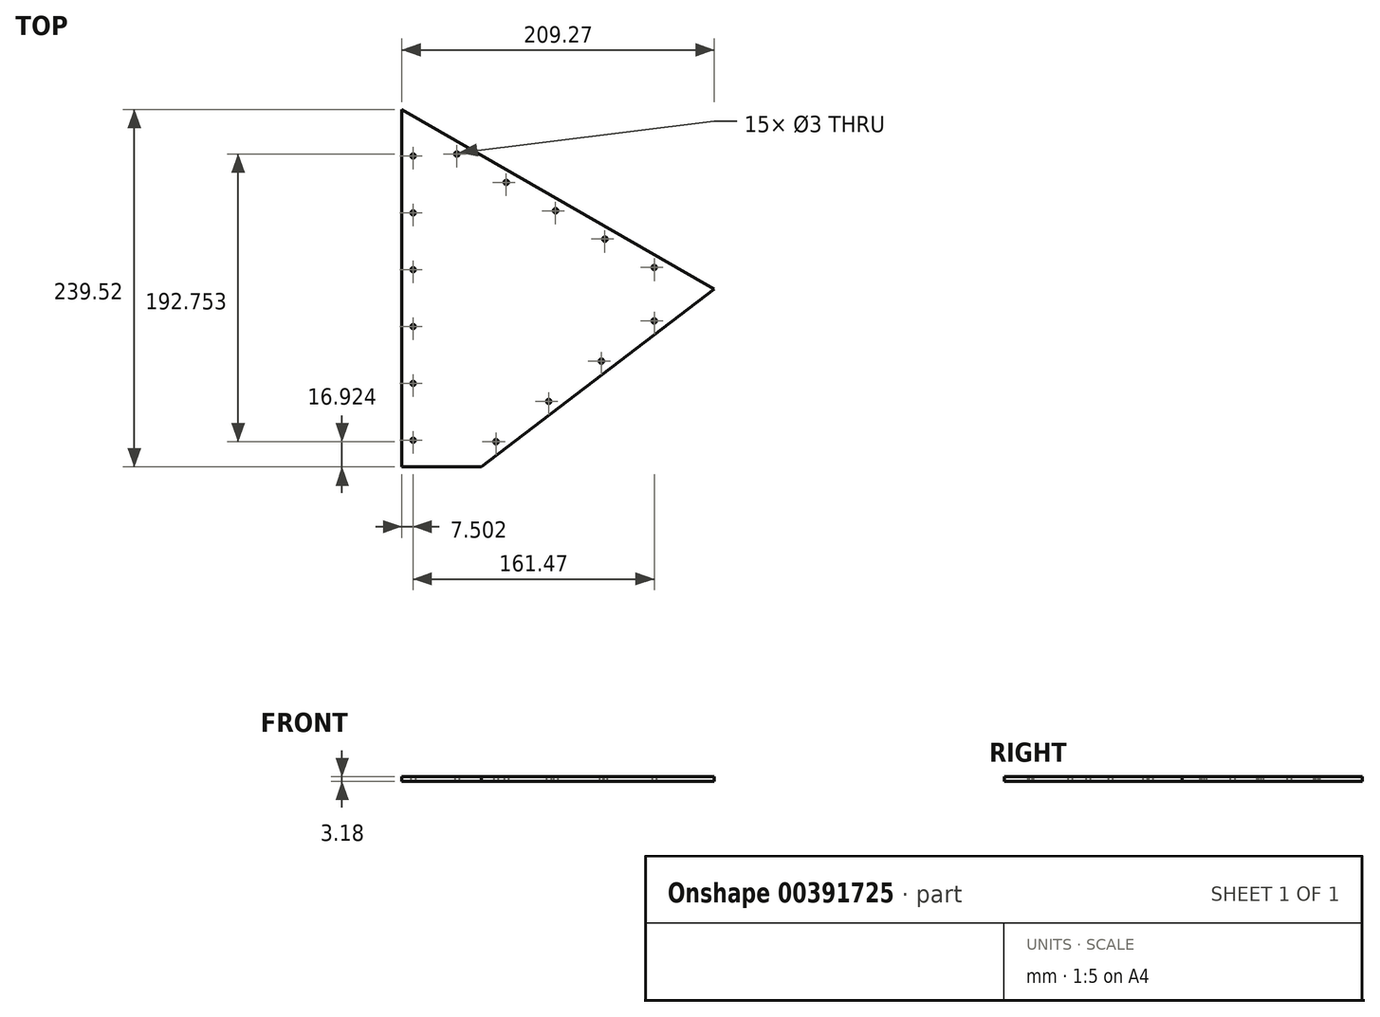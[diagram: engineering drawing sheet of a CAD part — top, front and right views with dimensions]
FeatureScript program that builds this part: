
annotation { "Feature Type Name" : "Feature", "Feature Type Description" : "" }
export const myFeature = defineFeature(function(context is Context, id is Id, definition is map)
    precondition{}
    {
        {
            var Q0;
            Q0=qCreatedBy(makeId("Top.planeOp"),FACE);
            var sketch = newSketch(context, id + "F0", { "sketchPlane" : qUnion([Q0])});
            skLineSegment(sketch, "E0", {"start": v(-223.28, 109.14) * mm, "end": v(256.18, 164.08) * mm});
            skLineSegment(sketch, "E1", {"start": v(-223.28, 109.14) * mm, "end": v(-223.28, -202.01) * mm});
            skLineSegment(sketch, "E2", {"start": v(-223.28, -202.01) * mm, "end": v(256.18, 164.08) * mm});
            skLineSegment(sketch, "E3", {"start": v(-223.28, -202.01) * mm, "end": v(-223.28, 81.44) * mm, "construction": true});
            skSolve(sketch);
        }
        {
            var Q0;
            Q0=qCreatedBy(makeId("Top.planeOp"),FACE);
            var sketch = newSketch(context, id + "F1", { "sketchPlane" : qUnion([Q0])});
            skPoint(sketch, "E4.visualSharp", {"position": v(-223.28, -202.01) * mm});
            skCircle(sketch, "E5", {"center": v(-198.42, -128.65) * mm, "radius": 8 * mm});
            skLineSegment(sketch, "E6.0", {"start": v(-170.1, -161.41) * mm, "end": v(-14.01, -42.23) * mm});
            skLineSegment(sketch, "E7", {"start": v(-170.1, -161.41) * mm, "end": v(-223.28, -161.41) * mm});
            skLineSegment(sketch, "E8", {"start": v(-223.28, -161.41) * mm, "end": v(-223.28, 78.11) * mm});
            skLineSegment(sketch, "E9", {"start": v(-223.28, 78.11) * mm, "end": v(-14.01, -42.23) * mm});
            skPoint(sketch, "E10.orphan", {"position": v(256.18, 164.08) * mm});
            skLineSegment(sketch, "E11.0", {"start": v(-175.18, -146.41) * mm, "end": v(-41.04, -44) * mm});
            skLineSegment(sketch, "E11.1", {"start": v(-175.18, -146.41) * mm, "end": v(-208.28, -146.41) * mm});
            skLineSegment(sketch, "E11.2", {"start": v(-208.28, -146.41) * mm, "end": v(-208.28, 52.18) * mm});
            skLineSegment(sketch, "E11.3", {"start": v(-208.28, 52.18) * mm, "end": v(-41.04, -44) * mm});
            skCircle(sketch, "E12.1.0.0", {"center": v(-182.83, -119.65) * mm, "radius": 8 * mm});
            skCircle(sketch, "E12.2.0.0", {"center": v(-167.24, -110.65) * mm, "radius": 8 * mm});
            skCircle(sketch, "E12.3.0.0", {"center": v(-151.65, -101.65) * mm, "radius": 8 * mm});
            skCircle(sketch, "E12.4.0.0", {"center": v(-136.06, -92.65) * mm, "radius": 8 * mm});
            skCircle(sketch, "E12.5.0.0", {"center": v(-120.47, -83.65) * mm, "radius": 8 * mm});
            skCircle(sketch, "E12.6.0.0", {"center": v(-104.89, -74.65) * mm, "radius": 8 * mm});
            skCircle(sketch, "E12.7.0.0", {"center": v(-89.3, -65.65) * mm, "radius": 8 * mm});
            skLineSegment(sketch, "E12.direction1", {"start": v(-198.42, -128.65) * mm, "end": v(-182.83, -119.65) * mm, "construction": true});
            skCircle(sketch, "E13.1.0.0", {"center": v(-198.42, -110.65) * mm, "radius": 8 * mm});
            skCircle(sketch, "E13.2.0.0", {"center": v(-182.83, -101.65) * mm, "radius": 8 * mm});
            skCircle(sketch, "E13.3.0.0", {"center": v(-167.24, -92.65) * mm, "radius": 8 * mm});
            skCircle(sketch, "E13.4.0.0", {"center": v(-151.65, -83.65) * mm, "radius": 8 * mm});
            skCircle(sketch, "E13.5.0.0", {"center": v(-136.06, -74.65) * mm, "radius": 8 * mm});
            skCircle(sketch, "E13.6.0.0", {"center": v(-120.47, -65.65) * mm, "radius": 8 * mm});
            skCircle(sketch, "E13.7.0.0", {"center": v(-104.89, -56.65) * mm, "radius": 8 * mm});
            skCircle(sketch, "E14.1.0.0", {"center": v(-198.42, -92.65) * mm, "radius": 8 * mm});
            skCircle(sketch, "E14.2.0.0", {"center": v(-182.83, -83.65) * mm, "radius": 8 * mm});
            skCircle(sketch, "E14.3.0.0", {"center": v(-167.24, -74.65) * mm, "radius": 8 * mm});
            skCircle(sketch, "E14.4.0.0", {"center": v(-151.65, -65.65) * mm, "radius": 8 * mm});
            skCircle(sketch, "E14.5.0.0", {"center": v(-136.06, -56.65) * mm, "radius": 8 * mm});
            skCircle(sketch, "E14.6.0.0", {"center": v(-120.47, -47.65) * mm, "radius": 8 * mm});
            skCircle(sketch, "E15", {"center": v(-198.42, -74.65) * mm, "radius": 8 * mm});
            skCircle(sketch, "E16.1.0.0", {"center": v(-182.83, -65.65) * mm, "radius": 8 * mm});
            skCircle(sketch, "E16.2.0.0", {"center": v(-167.24, -56.65) * mm, "radius": 8 * mm});
            skCircle(sketch, "E16.3.0.0", {"center": v(-151.65, -47.65) * mm, "radius": 8 * mm});
            skCircle(sketch, "E16.4.0.0", {"center": v(-136.06, -38.65) * mm, "radius": 8 * mm});
            skCircle(sketch, "E16.5.0.0", {"center": v(-120.47, -29.65) * mm, "radius": 8 * mm});
            skCircle(sketch, "E17", {"center": v(-198.42, -56.65) * mm, "radius": 8 * mm});
            skCircle(sketch, "E18.1.0.0", {"center": v(-182.83, -47.65) * mm, "radius": 8 * mm});
            skCircle(sketch, "E18.2.0.0", {"center": v(-167.24, -38.65) * mm, "radius": 8 * mm});
            skCircle(sketch, "E18.3.0.0", {"center": v(-151.65, -29.65) * mm, "radius": 8 * mm});
            skCircle(sketch, "E18.4.0.0", {"center": v(-136.06, -20.65) * mm, "radius": 8 * mm});
            skCircle(sketch, "E19", {"center": v(-198.42, -38.65) * mm, "radius": 8 * mm});
            skCircle(sketch, "E20.1.0.0", {"center": v(-182.83, -29.65) * mm, "radius": 8 * mm});
            skCircle(sketch, "E20.2.0.0", {"center": v(-167.24, -20.65) * mm, "radius": 8 * mm});
            skCircle(sketch, "E20.3.0.0", {"center": v(-151.65, -11.65) * mm, "radius": 8 * mm});
            skCircle(sketch, "E21", {"center": v(-198.42, -20.65) * mm, "radius": 8 * mm});
            skCircle(sketch, "E22.1.0.0", {"center": v(-182.83, -11.65) * mm, "radius": 8 * mm});
            skCircle(sketch, "E22.2.0.0", {"center": v(-167.24, -2.65) * mm, "radius": 8 * mm});
            skCircle(sketch, "E22.3.0.0", {"center": v(-151.65, 6.35) * mm, "radius": 8 * mm});
            skLineSegment(sketch, "E23", {"start": v(-198.42, -128.65) * mm, "end": v(-198.42, -110.65) * mm});
            skLineSegment(sketch, "E24", {"start": v(-198.42, -92.65) * mm, "end": v(-198.42, -110.65) * mm});
            skLineSegment(sketch, "E25", {"start": v(-198.42, -92.65) * mm, "end": v(-198.42, -74.65) * mm});
            skLineSegment(sketch, "E26", {"start": v(-198.42, -56.65) * mm, "end": v(-198.42, -38.65) * mm});
            skLineSegment(sketch, "E27", {"start": v(-198.42, -20.65) * mm, "end": v(-182.83, -29.65) * mm});
            skLineSegment(sketch, "E28", {"start": v(-198.42, -38.65) * mm, "end": v(-198.42, -20.65) * mm});
            skLineSegment(sketch, "E29", {"start": v(-198.42, -56.65) * mm, "end": v(-198.42, -74.65) * mm});
            skLineSegment(sketch, "E30", {"start": v(-182.83, -119.65) * mm, "end": v(-182.83, -101.65) * mm});
            skLineSegment(sketch, "E31", {"start": v(-182.83, -83.65) * mm, "end": v(-182.83, -65.65) * mm});
            skLineSegment(sketch, "E32", {"start": v(-182.83, -47.65) * mm, "end": v(-182.83, -29.65) * mm});
            skLineSegment(sketch, "E33", {"start": v(-182.83, -11.65) * mm, "end": v(-182.83, -29.65) * mm});
            skLineSegment(sketch, "E34", {"start": v(-182.83, -11.65) * mm, "end": v(-167.24, -20.65) * mm});
            skLineSegment(sketch, "E35", {"start": v(-167.24, -38.65) * mm, "end": v(-167.24, -20.65) * mm});
            skLineSegment(sketch, "E36", {"start": v(-167.24, -38.65) * mm, "end": v(-167.24, -56.65) * mm});
            skLineSegment(sketch, "E37", {"start": v(-167.24, -56.65) * mm, "end": v(-167.24, -74.65) * mm});
            skLineSegment(sketch, "E38", {"start": v(-167.24, -74.65) * mm, "end": v(-167.24, -92.65) * mm});
            skLineSegment(sketch, "E39", {"start": v(-167.24, -92.65) * mm, "end": v(-167.24, -110.65) * mm});
            skLineSegment(sketch, "E40", {"start": v(-182.83, -101.65) * mm, "end": v(-182.83, -83.65) * mm});
            skLineSegment(sketch, "E41", {"start": v(-182.83, -65.65) * mm, "end": v(-182.83, -47.65) * mm});
            skLineSegment(sketch, "E42", {"start": v(-198.42, -110.65) * mm, "end": v(-182.83, -119.65) * mm});
            skLineSegment(sketch, "E43", {"start": v(-151.65, 6.35) * mm, "end": v(-151.65, -101.65) * mm});
            skLineSegment(sketch, "E44", {"start": v(-167.24, -2.65) * mm, "end": v(-120.47, -29.65) * mm});
            skLineSegment(sketch, "E45", {"start": v(-167.24, -2.65) * mm, "end": v(-167.24, -20.65) * mm});
            skLineSegment(sketch, "E46", {"start": v(-136.06, -20.65) * mm, "end": v(-136.06, -92.65) * mm});
            skLineSegment(sketch, "E47", {"start": v(-198.42, -110.65) * mm, "end": v(-104.89, -56.65) * mm});
            skLineSegment(sketch, "E48", {"start": v(-182.83, -11.65) * mm, "end": v(-89.3, -65.65) * mm});
            skLineSegment(sketch, "E49", {"start": v(-198.42, -92.65) * mm, "end": v(-120.47, -47.65) * mm});
            skLineSegment(sketch, "E50", {"start": v(-198.42, -74.65) * mm, "end": v(-120.47, -29.65) * mm});
            skLineSegment(sketch, "E51", {"start": v(-120.47, -29.65) * mm, "end": v(-120.47, -83.65) * mm});
            skLineSegment(sketch, "E52", {"start": v(-198.42, -56.65) * mm, "end": v(-136.06, -20.65) * mm});
            skLineSegment(sketch, "E53", {"start": v(-198.42, -128.65) * mm, "end": v(-89.3, -65.65) * mm});
            skLineSegment(sketch, "E54", {"start": v(-198.42, -38.65) * mm, "end": v(-151.65, -11.65) * mm});
            skLineSegment(sketch, "E55", {"start": v(-198.42, -20.65) * mm, "end": v(-151.65, 6.35) * mm});
            skCircle(sketch, "E56", {"center": v(-198.42, -2.65) * mm, "radius": 8 * mm});
            skCircle(sketch, "E57.1.0.0", {"center": v(-182.83, 6.35) * mm, "radius": 8 * mm});
            skCircle(sketch, "E57.2.0.0", {"center": v(-167.24, 15.35) * mm, "radius": 8 * mm});
            skCircle(sketch, "E58", {"center": v(-198.42, 15.35) * mm, "radius": 8 * mm});
            skCircle(sketch, "E59.1.0.0", {"center": v(-182.83, 24.35) * mm, "radius": 8 * mm});
            skCircle(sketch, "E59.3.0.0", {"center": v(-198.42, 33.35) * mm, "radius": 8 * mm});
            skLineSegment(sketch, "E60", {"start": v(-198.42, 33.35) * mm, "end": v(-198.42, -38.65) * mm});
            skLineSegment(sketch, "E61", {"start": v(-198.42, -2.65) * mm, "end": v(-182.83, -11.65) * mm});
            skLineSegment(sketch, "E62", {"start": v(-198.42, 15.35) * mm, "end": v(-167.24, -2.65) * mm});
            skLineSegment(sketch, "E63", {"start": v(-198.42, 33.35) * mm, "end": v(-151.65, 6.35) * mm});
            skLineSegment(sketch, "E64", {"start": v(-198.42, 15.35) * mm, "end": v(-182.83, 24.35) * mm});
            skCircle(sketch, "E65.5.0.0", {"center": v(-73.7, -56.65) * mm, "radius": 8 * mm});
            skCircle(sketch, "E66.4.0.0", {"center": v(-89.3, -47.65) * mm, "radius": 8 * mm});
            skCircle(sketch, "E67.3.0.0", {"center": v(-104.89, -38.65) * mm, "radius": 8 * mm});
            skLineSegment(sketch, "E68", {"start": v(-120.47, -29.65) * mm, "end": v(-73.7, -56.65) * mm});
            skLineSegment(sketch, "E69", {"start": v(-104.89, -38.65) * mm, "end": v(-120.47, -47.65) * mm});
            skLineSegment(sketch, "E70", {"start": v(-89.3, -47.65) * mm, "end": v(-104.89, -56.65) * mm});
            skLineSegment(sketch, "E71", {"start": v(-198.42, -2.65) * mm, "end": v(-167.24, 15.35) * mm});
            skLineSegment(sketch, "E72", {"start": v(-73.7, -56.65) * mm, "end": v(-89.3, -65.65) * mm});
            skCircle(sketch, "E73.3.0.0", {"center": v(-120.47, -11.65) * mm, "radius": 8 * mm});
            skCircle(sketch, "E74.2.0.0", {"center": v(-136.06, -2.65) * mm, "radius": 8 * mm});
            skLineSegment(sketch, "E75", {"start": v(-120.47, -11.65) * mm, "end": v(-151.65, 6.35) * mm});
            skLineSegment(sketch, "E76", {"start": v(-120.47, -11.65) * mm, "end": v(-120.47, -29.65) * mm});
            skLineSegment(sketch, "E77", {"start": v(-136.06, -2.65) * mm, "end": v(-136.06, -20.65) * mm});
            skSolve(sketch);
        }
        {
            var Q0;
            Q0=makeQuery(id+"F0.imprint","IMPRINT",FACE,{"disambiguationData":[TD([[makeQuery(id+"F0.imprint","IMPRINT",EDGE,{"derivedFrom":sQuery(id+"F0.wireOp",EDGE,"E0")}),-1.0]])]});
            var sketch = newSketch(context, id + "F2", { "sketchPlane" : qUnion([Q0])});
            skLineSegment(sketch, "E78.0", {"start": v(-223.28, 78.11) * mm, "end": v(-14.01, -42.23) * mm});
            skLineSegment(sketch, "E79.0", {"start": v(-223.28, -161.41) * mm, "end": v(-223.28, 78.11) * mm});
            skLineSegment(sketch, "E80.0", {"start": v(-170.1, -161.41) * mm, "end": v(-223.28, -161.41) * mm});
            skLineSegment(sketch, "E81.0", {"start": v(-170.1, -161.41) * mm, "end": v(-14.01, -42.23) * mm});
            skSolve(sketch);
        }
        {
            var Q0;
            Q0=qCreatedBy(makeId("Top.planeOp"),FACE);
            var sketch = newSketch(context, id + "F3", { "sketchPlane" : qUnion([Q0])});
            skCircle(sketch, "E82", {"center": v(-160.3, -144.49) * mm, "radius": 1.5 * mm});
            skCircle(sketch, "E83", {"center": v(-124.97, -117.51) * mm, "radius": 1.5 * mm});
            skCircle(sketch, "E84", {"center": v(-89.64, -90.54) * mm, "radius": 1.5 * mm});
            skCircle(sketch, "E85", {"center": v(-54.3, -63.56) * mm, "radius": 1.5 * mm});
            skLineSegment(sketch, "E86", {"start": v(-54.3, -63.56) * mm, "end": v(-89.64, -90.54) * mm, "construction": true});
            skLineSegment(sketch, "E87", {"start": v(-89.64, -90.54) * mm, "end": v(-124.97, -117.51) * mm, "construction": true});
            skLineSegment(sketch, "E88", {"start": v(-124.97, -117.51) * mm, "end": v(-160.3, -144.49) * mm, "construction": true});
            skCircle(sketch, "E89", {"center": v(-54.3, -27.7) * mm, "radius": 1.5 * mm});
            skCircle(sketch, "E90", {"center": v(-87.34, -8.71) * mm, "radius": 1.5 * mm});
            skCircle(sketch, "E91", {"center": v(-120.36, 10.28) * mm, "radius": 1.5 * mm});
            skCircle(sketch, "E92", {"center": v(-153.4, 29.27) * mm, "radius": 1.5 * mm});
            skLineSegment(sketch, "E93", {"start": v(-153.4, 29.27) * mm, "end": v(-120.36, 10.28) * mm, "construction": true});
            skLineSegment(sketch, "E94", {"start": v(-120.36, 10.28) * mm, "end": v(-87.34, -8.71) * mm, "construction": true});
            skLineSegment(sketch, "E95", {"start": v(-87.34, -8.71) * mm, "end": v(-54.3, -27.7) * mm, "construction": true});
            skLineSegment(sketch, "E96", {"start": v(-54.3, -27.7) * mm, "end": v(-54.3, -63.56) * mm, "construction": true});
            skCircle(sketch, "E97", {"center": v(-215.78, -143.52) * mm, "radius": 1.5 * mm});
            skCircle(sketch, "E98", {"center": v(-215.78, -105.42) * mm, "radius": 1.5 * mm});
            skCircle(sketch, "E99", {"center": v(-215.78, -67.32) * mm, "radius": 1.5 * mm});
            skCircle(sketch, "E100", {"center": v(-215.78, -29.22) * mm, "radius": 1.5 * mm});
            skLineSegment(sketch, "E101", {"start": v(-215.78, -29.22) * mm, "end": v(-215.78, -67.32) * mm, "construction": true});
            skLineSegment(sketch, "E102", {"start": v(-215.78, -67.32) * mm, "end": v(-215.78, -105.42) * mm, "construction": true});
            skLineSegment(sketch, "E103", {"start": v(-215.78, -105.42) * mm, "end": v(-215.78, -143.52) * mm, "construction": true});
            skLineSegment(sketch, "E104", {"start": v(-215.78, -29.22) * mm, "end": v(-215.78, 8.88) * mm, "construction": true});
            skLineSegment(sketch, "E105", {"start": v(-215.78, 8.88) * mm, "end": v(-215.78, 46.98) * mm, "construction": true});
            skLineSegment(sketch, "E106", {"start": v(-186.42, 48.27) * mm, "end": v(-153.4, 29.27) * mm, "construction": true});
            skCircle(sketch, "E107", {"center": v(-215.78, 46.98) * mm, "radius": 1.5 * mm});
            skCircle(sketch, "E108", {"center": v(-186.42, 48.27) * mm, "radius": 1.5 * mm});
            skCircle(sketch, "E109", {"center": v(-215.78, 8.88) * mm, "radius": 1.5 * mm});
            skSolve(sketch);
        }
        {
            var Q0;
            Q0 = qSketchRegion(id + "F2", true);
            extrude(context, id + "F4", {"entities" : qUnion([Q0]), "depth" : 3.17 * mm});
        }
        {
            var Q0;
            Q0 = qSketchRegion(id + "F3", true);
            extrude(context, id + "F5", {"entities" : qUnion([Q0]), "operationType" : NewBodyOperationType.REMOVE, "depth" : 3.17 * mm});
        }
    });
